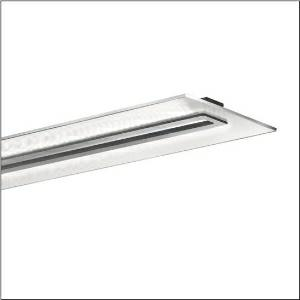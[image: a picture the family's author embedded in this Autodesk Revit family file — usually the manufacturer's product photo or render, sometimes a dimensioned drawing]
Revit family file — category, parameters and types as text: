
# Revit family: vega_r__11_5mn238dle0s3_873d
name_source: partatom
category: Lighting Fixtures
units: mm (PartAtom-declared; Revit-internal decimal feet)

## family parameters
Cut with Voids When Loaded = No
Host = Face
Light Source = No
Part Type = Normal
Room Calculation Point = No
Round Connector Dimension = Use Diameter
Shared = No

## types (1)
- --- (1 x LED 3000K / CRI = 80 (unbekannt), 7300 lm, 3000K)
    Apparent Load = 62 VA
    CIE Flux Codes = 61 86 97 62 100
    Color Rendering = 80
    Color Temperature = 3000K
    Default Elevation = 1800 mm
    Description = Vega® 11, office luminaire, primary light control with prismatic reflector, of PMMA, transparent prismatic structure, CAT 2 (L<= 1500cd/m²), light emission: direct/indirect distribution, primary light characteristic: symmetric, installation type: suspended mounting, surface-mounted, LED, rated luminous flux: 7.300lm, luminous efficacy: 118lm/W, light colour: 830, colour temperature: 3000K, control gear: DALI, with terminal, 3+2-pole, max. 2.5mm², mains connection: 230V, AC, 50Hz, connection cable inclusive, cable length: 1,5m, rated input power: 62W, luminaire housing, rectangular, rounded, of aluminium section, anodised, metallic grey (RAL 9006), length: 1.250mm, width: 350mm, height: 43mm, luminaire housing, lower part, of aluminium section, anodised, metallic grey (RAL 9006), of PC, grey, protection rating (complete): IP20, insulation class (complete): insulation class I (protective earthing), certification: CE, permissible operating ambient temperature: 0..+35°C, standard: EN 50419, packaging unit: 1 piece
    Height = 40 mm  [stored 0.131234 ft]
    Lamp = 1 x LED 3000K / CRI >= 80 (unbekannt)
    Lamp Light Flux = 7300 lm
    Lamp count = 1
    Length = 1250 mm
    Luminous efficacy = 118 lm/W
    Manufacturer = Siteco
    ModVariant = No
    Model = 5MN238DLE0S3
    Mounting Place = Ceiling
    Mounting Type = Pendant
    Number of Poles = 1
    OnlyDefault = Yes
    Power Factor = 1
    Product Name = Vega® 11
    Product group = office luminaire | ceiling pendant
    ProductGroupID = 903
    Protection Class = Protection class I
    Protection Degree = IP 20
    RLX_Detail_Level = 1
    RLX_Emergency_Light_Flux = 0 lm
    RLX_Emergency_Type = 0
    RLX_Emergency_Type_DB = No
    RlxData = <blob elided: 62609 chars, md5=b983665f>
    Socket = socket
    Standby Power = 0 W
    System Light Flux = 7300 lm
    System Power = 62 W
    Type Comments = factory setting: luminous flux: 100 % | dim-lin: 254 | 460 mA
    Type Image = l_1004807.jpg
    URL = http://relux.com
    VarID = @adj_220801
    Voltage = 0 V
    Weight = 0.00 kg
    Width = 350 mm

note: [stored X ft] marks values corroborated as IEEE doubles in the binary element streams (Revit-internal decimal feet)

## geometry (parser evidence)
native form markers: Blend x4, Sweep x14
no freeform markers — native parametric forms only
